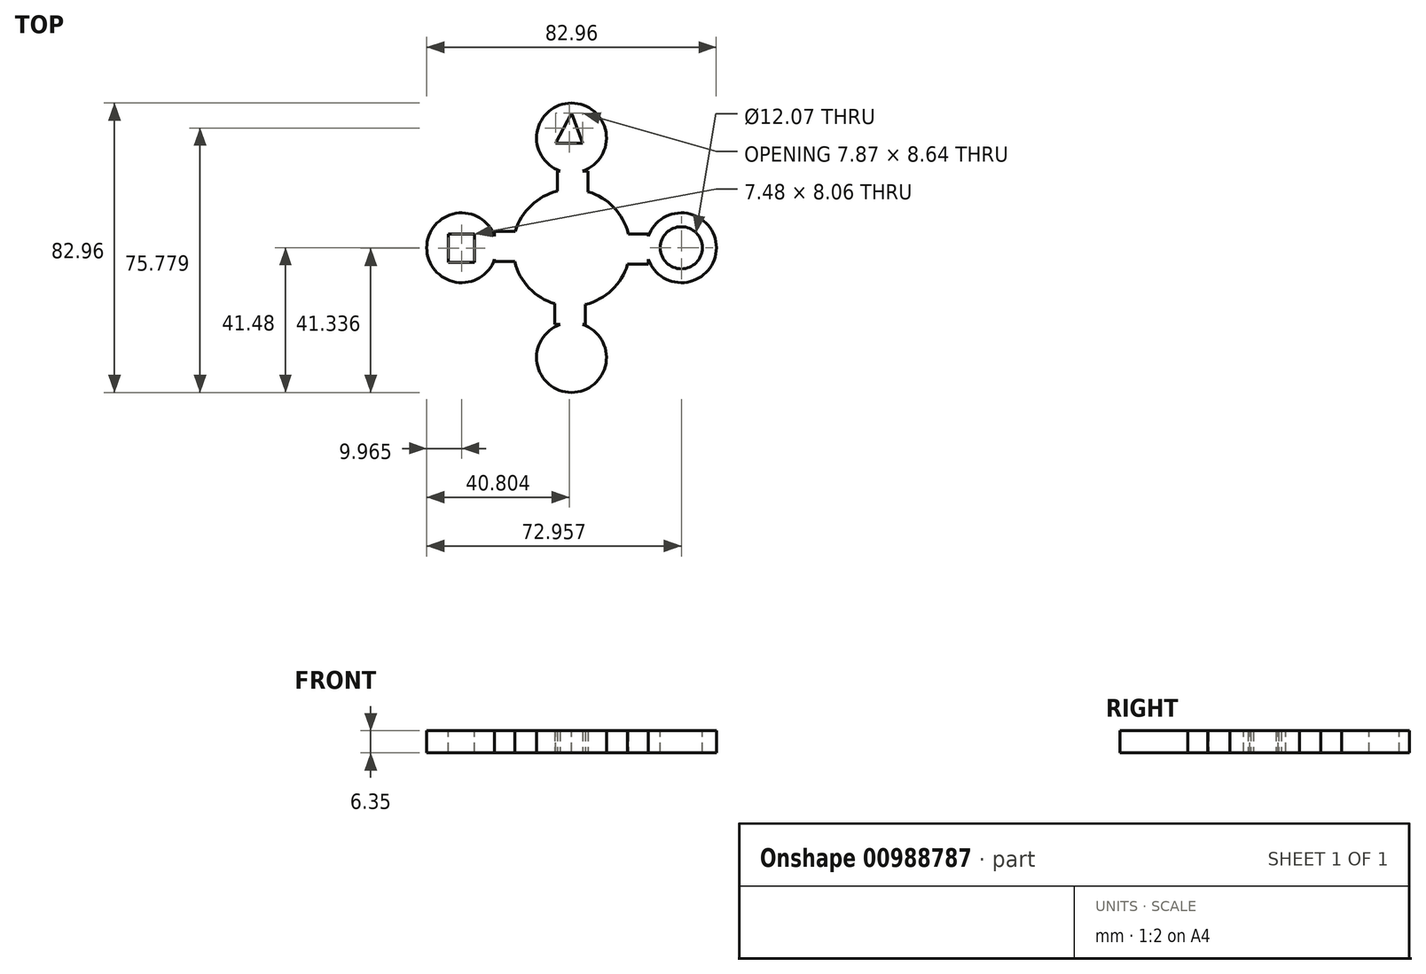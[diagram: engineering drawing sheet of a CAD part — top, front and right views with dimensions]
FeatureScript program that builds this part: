
annotation { "Feature Type Name" : "Feature", "Feature Type Description" : "" }
export const myFeature = defineFeature(function(context is Context, id is Id, definition is map)
    precondition{}
    {
        {
            var Q0;
            Q0=qCreatedBy(makeId("Top.planeOp"),FACE);
            var sketch = newSketch(context, id + "F0", { "sketchPlane" : qUnion([Q0])});
            skCircle(sketch, "E0", {"center": v(0, 0) * mm, "radius": 16.75 * mm});
            skLineSegment(sketch, "E1", {"start": v(-4, 16.27) * mm, "end": v(-4, 22.02) * mm});
            skLineSegment(sketch, "E2", {"start": v(-4, 22.02) * mm, "end": v(4.75, 22.02) * mm});
            skLineSegment(sketch, "E3", {"start": v(4.75, 22.02) * mm, "end": v(4.75, 16.06) * mm});
            skLineSegment(sketch, "E4", {"start": v(4.75, 16.06) * mm, "end": v(-4, 16.27) * mm});
            skLineSegment(sketch, "E5.1.0", {"start": v(-16.27, -4) * mm, "end": v(-22.02, -4) * mm});
            skLineSegment(sketch, "E5.1.1", {"start": v(-16.06, 4.75) * mm, "end": v(-16.27, -4) * mm});
            skLineSegment(sketch, "E5.1.2", {"start": v(-22.02, -4) * mm, "end": v(-22.02, 4.75) * mm});
            skLineSegment(sketch, "E5.1.3", {"start": v(-22.02, 4.75) * mm, "end": v(-16.06, 4.75) * mm});
            skLineSegment(sketch, "E5.2.0", {"start": v(4, -16.27) * mm, "end": v(4, -22.02) * mm});
            skLineSegment(sketch, "E5.2.1", {"start": v(-4.75, -16.06) * mm, "end": v(4, -16.27) * mm});
            skLineSegment(sketch, "E5.2.2", {"start": v(4, -22.02) * mm, "end": v(-4.75, -22.02) * mm});
            skLineSegment(sketch, "E5.2.3", {"start": v(-4.75, -22.02) * mm, "end": v(-4.75, -16.06) * mm});
            skLineSegment(sketch, "E5.3.0", {"start": v(16.27, 4) * mm, "end": v(22.02, 4) * mm});
            skLineSegment(sketch, "E5.3.1", {"start": v(16.06, -4.75) * mm, "end": v(16.27, 4) * mm});
            skLineSegment(sketch, "E5.3.2", {"start": v(22.02, 4) * mm, "end": v(22.02, -4.75) * mm});
            skLineSegment(sketch, "E5.3.3", {"start": v(22.02, -4.75) * mm, "end": v(16.06, -4.75) * mm});
            skCircle(sketch, "E6", {"center": v(0, 31.48) * mm, "radius": 10 * mm});
            skCircle(sketch, "E7.1.0", {"center": v(-31.48, 0) * mm, "radius": 10 * mm});
            skCircle(sketch, "E7.2.0", {"center": v(0, -31.48) * mm, "radius": 10 * mm});
            skCircle(sketch, "E7.3.0", {"center": v(31.48, 0) * mm, "radius": 10 * mm});
            skSolve(sketch);
        }
        {
            var Q0;
            Q0 = qSketchRegion(id + "F0", true);
            extrude(context, id + "F1", {"entities" : qUnion([Q0]), "depth" : 6.35 * mm, "offsetDistance" : 25.4 * mm});
        }
        {
            var Q0;
            Q0=makeQuery(id+"F1.opExtrude","CAP_FACE",FACE,{"disambiguationData":[OSD([sQuery(id+"F0.wireOp",EDGE,"E0"),sQuery(id+"F0.wireOp",EDGE,"E1"),sQuery(id+"F0.wireOp",EDGE,"E2"),sQuery(id+"F0.wireOp",EDGE,"E3"),sQuery(id+"F0.wireOp",EDGE,"E5.1.0"),sQuery(id+"F0.wireOp",EDGE,"E5.1.2"),sQuery(id+"F0.wireOp",EDGE,"E5.1.3"),sQuery(id+"F0.wireOp",EDGE,"E5.2.0"),sQuery(id+"F0.wireOp",EDGE,"E5.2.2"),sQuery(id+"F0.wireOp",EDGE,"E5.2.3"),sQuery(id+"F0.wireOp",EDGE,"E5.3.0"),sQuery(id+"F0.wireOp",EDGE,"E5.3.2"),sQuery(id+"F0.wireOp",EDGE,"E5.3.3"),sQuery(id+"F0.wireOp",EDGE,"E6"),sQuery(id+"F0.wireOp",EDGE,"E7.1.0"),sQuery(id+"F0.wireOp",EDGE,"E7.2.0"),sQuery(id+"F0.wireOp",EDGE,"E7.3.0")])],"isStart":false});
            var sketch = newSketch(context, id + "F2", { "sketchPlane" : qUnion([Q0])});
            skLineSegment(sketch, "E8", {"start": v(0, 38.62) * mm, "end": v(-4.61, 29.98) * mm});
            skLineSegment(sketch, "E9", {"start": v(-4.61, 29.98) * mm, "end": v(3.26, 29.98) * mm});
            skLineSegment(sketch, "E10", {"start": v(3.26, 29.98) * mm, "end": v(0, 38.62) * mm});
            skCircle(sketch, "E11", {"center": v(31.48, 0) * mm, "radius": 6.03 * mm});
            skLineSegment(sketch, "E12.bottom", {"start": v(-35.26, 3.89) * mm, "end": v(-27.77, 3.89) * mm});
            skLineSegment(sketch, "E12.top", {"start": v(-35.26, -4.17) * mm, "end": v(-27.77, -4.17) * mm});
            skLineSegment(sketch, "E12.left", {"start": v(-35.26, 3.89) * mm, "end": v(-35.26, -4.17) * mm});
            skLineSegment(sketch, "E12.right", {"start": v(-27.77, 3.89) * mm, "end": v(-27.77, -4.17) * mm});
            skLineSegment(sketch, "E13", {"start": v(4, -27.49) * mm, "end": v(-3.6, -35.26) * mm});
            skLineSegment(sketch, "E14", {"start": v(-3.26, -27.77) * mm, "end": v(4, -34.86) * mm});
            skSolve(sketch);
        }
        {
            var Q0;
            Q0=makeQuery(id+"F2.imprint","IMPRINT",FACE,{"disambiguationData":[TD([[makeQuery(id+"F2.imprint","IMPRINT",EDGE,{"derivedFrom":sQuery(id+"F2.wireOp",EDGE,"E12.bottom")}),-1.0]])]});
            extrude(context, id + "F3", {"entities" : qUnion([Q0]), "operationType" : NewBodyOperationType.REMOVE, "oppositeDirection" : true, "depth" : 59.44 * mm, "offsetDistance" : 25.4 * mm});
        }
        {
            var Q0;
            Q0=makeQuery(id+"F2.imprint","IMPRINT",FACE,{"disambiguationData":[TD([[makeQuery(id+"F2.imprint","IMPRINT",EDGE,{"derivedFrom":sQuery(id+"F2.wireOp",EDGE,"E11")}),1.0]])]});
            var Q1;
            Q1=makeQuery(id+"F2.imprint","IMPRINT",FACE,{"disambiguationData":[TD([[makeQuery(id+"F2.imprint","IMPRINT",EDGE,{"derivedFrom":sQuery(id+"F2.wireOp",EDGE,"E8")}),1.0]])]});
            extrude(context, id + "F4", {"entities" : qUnion([Q0, Q1]), "operationType" : NewBodyOperationType.REMOVE, "oppositeDirection" : true, "depth" : 108.46 * mm, "offsetDistance" : 25.4 * mm});
        }
    });
